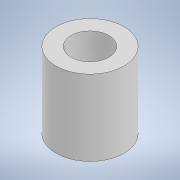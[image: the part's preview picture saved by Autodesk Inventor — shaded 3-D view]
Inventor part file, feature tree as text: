
AUTODESK INVENTOR PART (.ipt)
format: ipt  version: 2022.3 (Build 263350000, 350)  size: 95,232 bytes
history: native  units: mm
features: extrude x1, sketch x1
ambient origin geometry x8: Origin, YZ Plane, XZ Plane, XY Plane, X Axis, Y Axis, Z Axis, Center Point
bodies: Solid1 (feature_tree)
feature tree (2):
  extrude  "Extrusion1"  Depth=10.0mm
  sketch  "Sketch1"  dims[d0=5.0mm d1=2.0mm d2=10.0mm d3=0.0mm]
